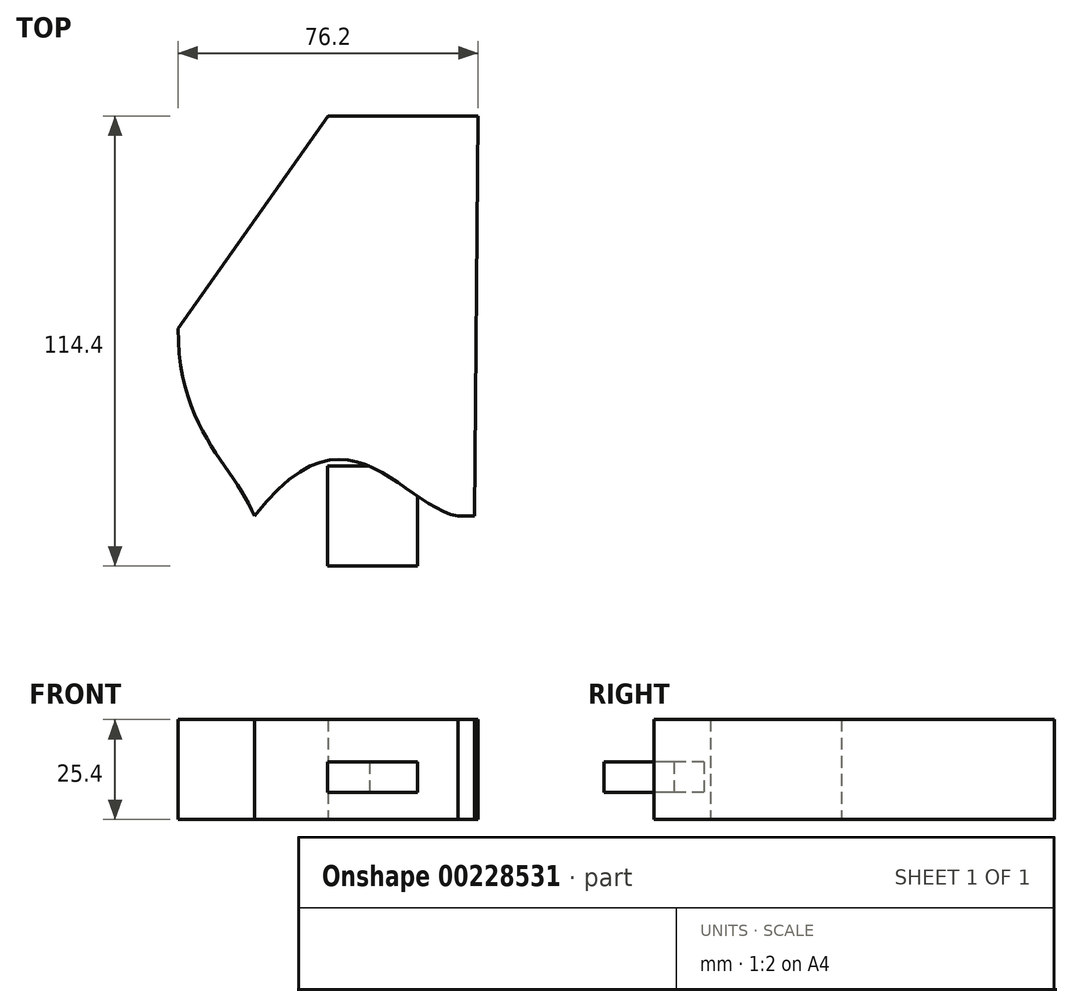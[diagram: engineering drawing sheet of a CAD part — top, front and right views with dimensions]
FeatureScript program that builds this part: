
annotation { "Feature Type Name" : "Feature", "Feature Type Description" : "" }
export const myFeature = defineFeature(function(context is Context, id is Id, definition is map)
    precondition{}
    {
        {
            var Q0;
            Q0=qCreatedBy(makeId("Top.planeOp"),FACE);
            var sketch = newSketch(context, id + "F0", { "sketchPlane" : qUnion([Q0])});
            skLineSegment(sketch, "E0.bottom", {"start": v(71.2, -0.1) * mm, "end": v(75.3, -0.1) * mm});
            skLineSegment(sketch, "E0.top", {"start": v(38.1, 101.6) * mm, "end": v(76.2, 101.6) * mm});
            skLineSegment(sketch, "E0.right", {"start": v(75.3, -0.1) * mm, "end": v(76.2, 101.6) * mm});
            skLineSegment(sketch, "E1", {"start": v(0, 47.57) * mm, "end": v(38.1, 101.6) * mm});
            skPoint(sketch, "E2.orphan", {"position": v(0, 101.6) * mm});
            skFitSpline(sketch, "E3", {"points": [v(0, 47.57) * mm, v(19.44, -0.1) * mm], "startDerivative": vector(0, -77.82) * mm, "endDerivative": vector(14.56, -37.52) * mm});
            skFitSpline(sketch, "E4", {"points": [v(19.44, -0.1) * mm, v(75.3, -0.1) * mm], "startDerivative": vector(77.81, 101.96) * mm, "endDerivative": vector(49.08, 9.44) * mm});
            skSolve(sketch);
        }
        {
            var Q0;
            Q0=makeQuery(id+"F0.imprint","IMPRINT",FACE,{"disambiguationData":[TD([[makeQuery(id+"F0.imprint","IMPRINT",EDGE,{"derivedFrom":sQuery(id+"F0.wireOp",EDGE,"E0.bottom")}),1.0]])]});
            extrude(context, id + "F1", {"entities" : qUnion([Q0]), "depth" : 25.4 * mm});
        }
        {
            var Q0;
            Q0=makeQuery(id+"F1.opExtrude","SWEPT_FACE",FACE,{"disambiguationData":[OSD([sQuery(id+"F0.wireOp",EDGE,"E0.bottom")])]});
            var sketch = newSketch(context, id + "F2", { "sketchPlane" : qUnion([Q0])});
            skLineSegment(sketch, "E5.bottom", {"start": v(38.05, 14.6) * mm, "end": v(60.86, 14.6) * mm});
            skLineSegment(sketch, "E5.top", {"start": v(38.05, 6.95) * mm, "end": v(60.86, 6.95) * mm});
            skLineSegment(sketch, "E5.left", {"start": v(38.05, 14.6) * mm, "end": v(38.05, 6.95) * mm});
            skLineSegment(sketch, "E5.right", {"start": v(60.86, 14.6) * mm, "end": v(60.86, 6.95) * mm});
            skSolve(sketch);
        }
        {
            var Q0;
            Q0=makeQuery(id+"F2.imprint","IMPRINT",FACE,{"disambiguationData":[TD([[makeQuery(id+"F2.imprint","IMPRINT",EDGE,{"derivedFrom":sQuery(id+"F2.wireOp",EDGE,"E5.bottom")}),-1.0]])]});
            extrude(context, id + "F3", {"entities" : qUnion([Q0]), "operationType" : NewBodyOperationType.ADD, "endBound" : BoundingType.SYMMETRIC, "oppositeDirection" : true, "depth" : 25.4 * mm});
        }
    });
